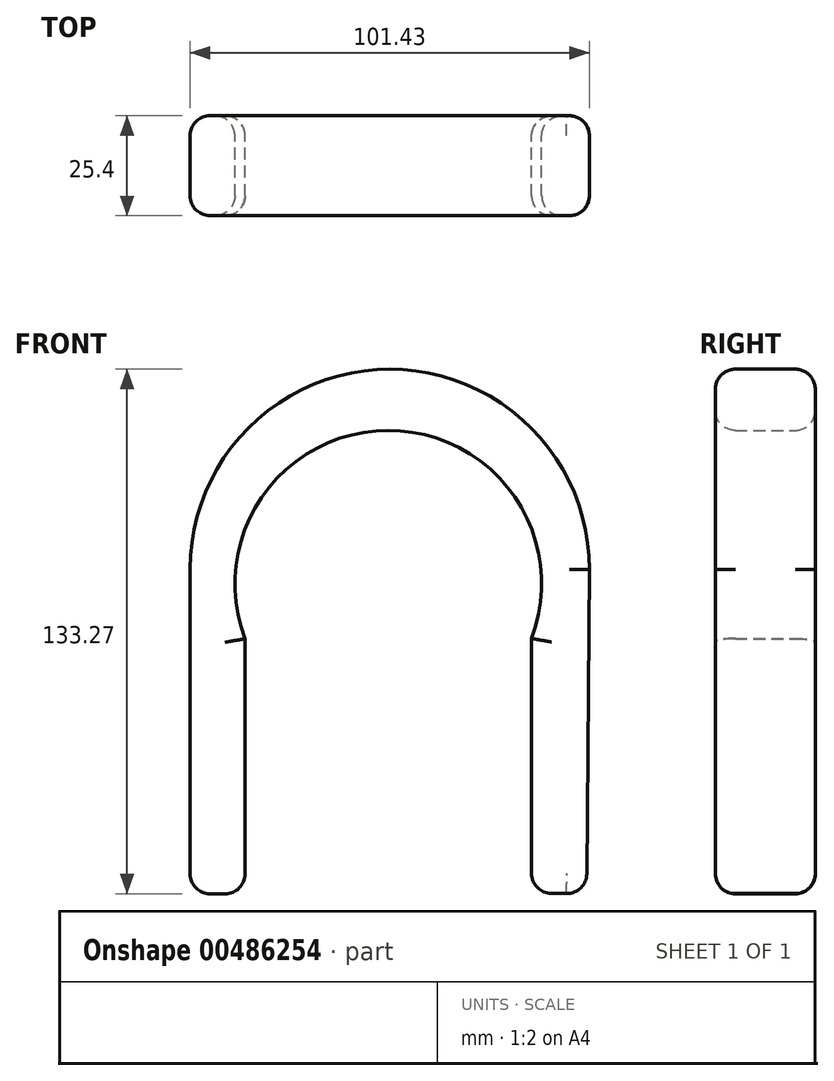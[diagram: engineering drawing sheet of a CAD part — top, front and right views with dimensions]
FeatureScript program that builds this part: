
annotation { "Feature Type Name" : "Feature", "Feature Type Description" : "" }
export const myFeature = defineFeature(function(context is Context, id is Id, definition is map)
    precondition{}
    {
        {
            var Q0;
            Q0=qCreatedBy(makeId("Front.planeOp"),FACE);
            var sketch = newSketch(context, id + "F0", { "sketchPlane" : qUnion([Q0])});
            skLineSegment(sketch, "E0", {"start": v(-100.73, -49.34) * mm, "end": v(-100.73, 33.21) * mm});
            skLineSegment(sketch, "E1", {"start": v(0.7, 33.05) * mm, "end": v(0, -49.33) * mm});
            skLineSegment(sketch, "E2", {"start": v(-100.73, -49.34) * mm, "end": v(-86.76, -49.34) * mm});
            skLineSegment(sketch, "E3", {"start": v(0, -49.33) * mm, "end": v(-13.97, -49.22) * mm});
            skLineSegment(sketch, "E4", {"start": v(-86.76, -49.34) * mm, "end": v(-86.76, 15.46) * mm});
            skLineSegment(sketch, "E5", {"start": v(-13.97, -49.22) * mm, "end": v(-13.97, 15.52) * mm});
            skPoint(sketch, "E6.visualSharp", {"position": v(-86.76, 34.48) * mm});
            skPoint(sketch, "E7.visualSharp", {"position": v(-13.97, 34.6) * mm});
            skPoint(sketch, "E8.visualSharp", {"position": v(0.87, 52.26) * mm});
            skPoint(sketch, "E9.visualSharp", {"position": v(-100.73, 52.26) * mm});
            skArc(sketch, "E10", {"start": v(0.7, 33.05) * mm, "mid": v(-49.94, 83.93) * mm, "end": v(-100.73, 33.21) * mm});
            skArc(sketch, "E11", {"start": v(-13.97, 15.52) * mm, "mid": v(-50.4, 68.38) * mm, "end": v(-86.76, 15.46) * mm});
            skSolve(sketch);
        }
        {
            var Q0;
            Q0=makeQuery(id+"F0.imprint","IMPRINT",FACE,{"disambiguationData":[TD([[makeQuery(id+"F0.imprint","IMPRINT",EDGE,{"derivedFrom":sQuery(id+"F0.wireOp",EDGE,"E0")}),-1.0]])]});
            extrude(context, id + "F1", {"entities" : qUnion([Q0]), "depth" : 25.4 * mm});
        }
        {
            var Q0;
            Q0=makeQuery(id+"F1.opExtrude","SWEPT_EDGE",EDGE,{"disambiguationData":[OSD([sQuery(id+"F0.wireOp",EDGE,"E2"),sQuery(id+"F0.wireOp",EDGE,"E4")])]});
            fillet(context, id + "F2", {"entities" : qUnion([Q0]), "radius" : 5.08 * mm, "tangentPropagation" : true, "allowEdgeOverflow" : false});
        }
        {
            var Q0;
            Q0=makeQuery(id+"F1.opExtrude","SWEPT_EDGE",EDGE,{"disambiguationData":[OSD([sQuery(id+"F0.wireOp",EDGE,"E3"),sQuery(id+"F0.wireOp",EDGE,"E5")])]});
            fillet(context, id + "F3", {"entities" : qUnion([Q0]), "radius" : 5.08 * mm, "tangentPropagation" : true, "allowEdgeOverflow" : false});
        }
        {
            var Q0;
            Q0=makeQuery(id+"F0.imprint","IMPRINT",FACE,{"disambiguationData":[TD([[makeQuery(id+"F0.imprint","IMPRINT",EDGE,{"derivedFrom":sQuery(id+"F0.wireOp",EDGE,"E0")}),-1.0]])]});
            extrude(context, id + "F4", {"entities" : qUnion([Q0]), "operationType" : NewBodyOperationType.ADD, "depth" : 25.4 * mm});
        }
        {
            var Q0;
            Q0=makeQuery(id+"F4.opExtrude","CAP_EDGE",EDGE,{"disambiguationData":[OSD([sQuery(id+"F0.wireOp",EDGE,"E0")])],"isStart":false});
            var Q1;
            Q1=makeQuery(id+"F4.opExtrude","CAP_EDGE",EDGE,{"disambiguationData":[OSD([sQuery(id+"F0.wireOp",EDGE,"cV8WoCmZ-d3HI-jRy4-joKu-v5l6YuiHuHAf")])],"isStart":false});
            var Q2;
            Q2=makeQuery(id+"F4.opExtrude","CAP_EDGE",EDGE,{"disambiguationData":[OSD([sQuery(id+"F0.wireOp",EDGE,"E9.filletArc")])],"isStart":false});
            var Q3;
            Q3=makeQuery(id+"F4.opExtrude","CAP_EDGE",EDGE,{"disambiguationData":[OSD([sQuery(id+"F0.wireOp",EDGE,"E8.filletArc")])],"isStart":false});
            var Q4;
            Q4=makeQuery(id+"F4.opExtrude","CAP_EDGE",EDGE,{"disambiguationData":[OSD([sQuery(id+"F0.wireOp",EDGE,"E1")])],"isStart":false});
            var Q5;
            Q5=makeQuery(id+"F4.opExtrude","SWEPT_EDGE",EDGE,{"disambiguationData":[OSD([sQuery(id+"F0.wireOp",EDGE,"E2"),sQuery(id+"F0.wireOp",EDGE,"E4")])]});
            var Q6;
            Q6=makeQuery(id+"F4.opExtrude","SWEPT_EDGE",EDGE,{"disambiguationData":[OSD([sQuery(id+"F0.wireOp",EDGE,"E0"),sQuery(id+"F0.wireOp",EDGE,"E2")])]});
            var Q7;
            Q7=makeQuery(id+"F4.opExtrude","SWEPT_EDGE",EDGE,{"disambiguationData":[OSD([sQuery(id+"F0.wireOp",EDGE,"E3"),sQuery(id+"F0.wireOp",EDGE,"E5")])]});
            var Q8;
            Q8=makeQuery(id+"F4.opExtrude","SWEPT_EDGE",EDGE,{"disambiguationData":[OSD([sQuery(id+"F0.wireOp",EDGE,"E1"),sQuery(id+"F0.wireOp",EDGE,"E3")])]});
            fillet(context, id + "F5", {"entities" : qUnion([Q0, Q1, Q2, Q3, Q4, Q5, Q6, Q7, Q8]), "radius" : 5.08 * mm, "tangentPropagation" : true, "allowEdgeOverflow" : false});
        }
        {
            var Q0;
            {var subQ0=sQuery(id+"F0.wireOp",EDGE,"E5");Q0=makeQuery(id+"F4.boolean.opBoolean","MERGE",EDGE,{"derivedFrom":[makeQuery(id+"F1.opExtrude","CAP_EDGE",EDGE,{"disambiguationData":[OSD([subQ0])],"isStart":false}),makeQuery(id+"F4.opExtrude","CAP_EDGE",EDGE,{"disambiguationData":[OSD([subQ0])],"isStart":false})]});}
            var Q1;
            Q1=makeQuery(id+"F1.opExtrude","CAP_EDGE",EDGE,{"disambiguationData":[OSD([sQuery(id+"F0.wireOp",EDGE,"E11")])],"isStart":false});
            var Q2;
            {var subQ0=sQuery(id+"F0.wireOp",EDGE,"E4");Q2=makeQuery(id+"F4.boolean.opBoolean","MERGE",EDGE,{"derivedFrom":[makeQuery(id+"F1.opExtrude","CAP_EDGE",EDGE,{"disambiguationData":[OSD([subQ0])],"isStart":false}),makeQuery(id+"F4.opExtrude","CAP_EDGE",EDGE,{"disambiguationData":[OSD([subQ0])],"isStart":false})]});}
            fillet(context, id + "F6", {"entities" : qUnion([Q0, Q1, Q2]), "radius" : 5.08 * mm, "tangentPropagation" : true, "allowEdgeOverflow" : false});
        }
        {
            var Q0;
            Q0=makeQuery(id+"F1.opExtrude","CAP_EDGE",EDGE,{"disambiguationData":[OSD([sQuery(id+"F0.wireOp",EDGE,"E10")])],"isStart":false});
            var Q1;
            Q1=makeQuery(id+"F1.opExtrude","CAP_EDGE",EDGE,{"disambiguationData":[OSD([sQuery(id+"F0.wireOp",EDGE,"E1")])],"isStart":false});
            var Q2;
            Q2=makeQuery(id+"F1.opExtrude","CAP_EDGE",EDGE,{"disambiguationData":[OSD([sQuery(id+"F0.wireOp",EDGE,"E0")])],"isStart":false});
            fillet(context, id + "F7", {"entities" : qUnion([Q0, Q1, Q2]), "radius" : 5.08 * mm, "tangentPropagation" : true, "allowEdgeOverflow" : false});
        }
        {
            var Q0;
            Q0=makeQuery(id+"F1.opExtrude","CAP_EDGE",EDGE,{"disambiguationData":[OSD([sQuery(id+"F0.wireOp",EDGE,"E11")])],"isStart":true});
            var Q1;
            {var subQ0=sQuery(id+"F0.wireOp",EDGE,"E5");Q1=makeQuery(id+"F4.boolean.opBoolean","MERGE",EDGE,{"derivedFrom":[makeQuery(id+"F1.opExtrude","CAP_EDGE",EDGE,{"disambiguationData":[OSD([subQ0])],"isStart":true}),makeQuery(id+"F4.opExtrude","CAP_EDGE",EDGE,{"disambiguationData":[OSD([subQ0])],"isStart":true})]});}
            var Q2;
            {var subQ0=sQuery(id+"F0.wireOp",EDGE,"E4");Q2=makeQuery(id+"F4.boolean.opBoolean","MERGE",EDGE,{"derivedFrom":[makeQuery(id+"F1.opExtrude","CAP_EDGE",EDGE,{"disambiguationData":[OSD([subQ0])],"isStart":true}),makeQuery(id+"F4.opExtrude","CAP_EDGE",EDGE,{"disambiguationData":[OSD([subQ0])],"isStart":true})]});}
            fillet(context, id + "F8", {"entities" : qUnion([Q0, Q1, Q2]), "radius" : 5.08 * mm, "tangentPropagation" : true, "allowEdgeOverflow" : false});
        }
    });
